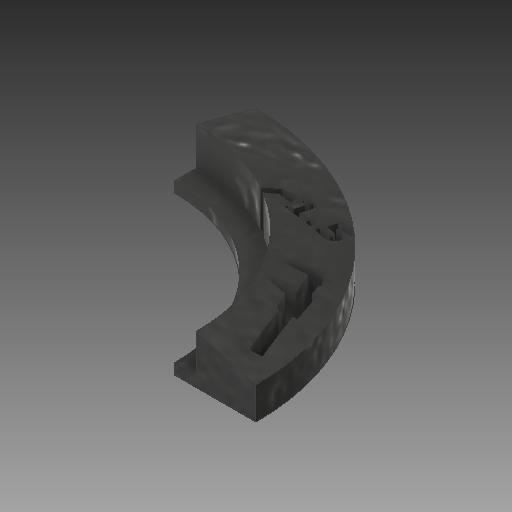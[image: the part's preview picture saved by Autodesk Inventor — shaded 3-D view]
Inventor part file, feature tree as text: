
AUTODESK INVENTOR PART (.ipt)
format: ipt  version: 2017 (Build 210142000, 142)  size: 505,856 bytes
history: native  units: in
note: dims shown in document units (in); Inventor stores cm internally (conversion verified against a paired STEP export)
features: reference x5, sketch x4, extrude x3, revolve x1, projected_geometry x1
ambient origin geometry x8: Origin, YZ Plane, XZ Plane, XY Plane, X Axis, Y Axis, Z Axis, Center Point
bodies: Solid1 (feature_tree)
feature tree (14):
  revolve  "Revolution1"  [1 undecoded]
  extrude  "Extrusion1"  Depth=0.05in
  extrude  "Extrusion2"  Depth=0.275in
  extrude  "Extrusion3"  Depth=0.025in
  sketch  "Sketch1"  dims[d0=0.8265in d1=0.175in]
  sketch  "Sketch2"  dims[d2=0.05in d3=0.1in]
  projected_geometry  "Projected Loop1"
  reference  "Reference1"
  reference  "Reference2"
  reference  "Reference3"
  sketch  "Sketch3"  dims[d4=0.15in d5=0.275in]
  reference  "Reference4"
  reference  "Reference5"
  sketch  "Sketch4"  dims[d6=90.0deg d7=1.55in d9=1.0in d11=0.025in d13=1.0in d14=0.025in d15=0.0125in d16=0.6536in d17=0.0125in d18=0.1in d19=0.05in d20=0.05in d21=0.025in d22=0.0125in d23=0.29in d24=0.0125in d25=0.1in d26=0.3in d27=0.1in d28=0.025in d29=0.015in d30=0.015in d31=0.035in d32=0.0175in d33=0.225in d34=0.1in d35=1.1in d36=0.035in d38=60.0deg d39=0.075in d40=0.0in d41=0.0in d42=0.125in d43=0.125in d44=0.04in d45=0.05in d46=0.04in d47=0.04in d49=0.025in d50=0.125in d51=0.5in d52=0.085in d53=0.1in d54=0.975in d55=0.025in d56=0.9812in d57=0.9812in d58=2.3363in d59=0.04in d60=0.025in d61=0.5in d62=0.0in d63=1.0in d64=0.0in]
note: 1 required parameter value undecoded (feature->parameter linkage not recoverable at this tier; creation-order binding heuristic only, values carry confidence <= 0.55)
